# Revit family: Gira_5333100
name_source: partatom
category: Elektroinstallationen
revit_build: Autodesk Revit 2017 (Build: 20160225_1515(x64)
units: mm (PartAtom-declared; Revit-internal decimal feet)

## family parameters
Basisbauteil = Fläche
Beim Laden mit Abzugskörper schneiden = Nein
Bemaßung runder Anschluss = Durchmesser verwenden
Beschriftungsausrichtung beibehalten = Nein
Gemeinsam genutzt = Nein
Raumberechnungspunkt = Nein
Teiletyp = Normal

## types (1)
- Gira_5333100
    Andere Bussysteme = ohne
    Anzahl der Kanäle = 3
    Ausführung = Wandsender komplett
    Ausführung der Oberfläche = glänzend
    BIM = https://media.stage.bim.site und Tasten.rfa
    Bauelement = Sys55_Abdeckung_Schalten und Tasten
    Beschreibung = eNet Funk Wandsender 3fach System 55, Wippen mit Beschriftungsfeld Klar   Reinweiß glänzend Merkmale: - Die eNet Funksender übertragen Schalt-, Dimm-, und Jalousiefahrbefehle an entsprechende eNet Funkempfänger. - Problemlose Erweiterung vorhandener Schalterkombinationen. - Die Montage kann ohne Aufputz-Gehäuse oder Gerätedose erfolgen. - Auf Wänden kann der Funk Wandsender mittels Schrauben befestigt bzw. auf glatten oder transparenten Oberflächen mit einer Montageplatte aufgeklebt werden. - Übertragung von Schalt-, Dimm-, Jalousiefahr- und Szenenbefehlen. - Umschaltfunktion, optimiert für die Ansteuerung von Tastaktoren. - Wippe als Kanal- oder Szenenfunktion einstellbar. - 2-farbige LED rechts und links der Tasten zur Signalisierung. - Batteriebetriebenes Gerät. Mit eNet Server einstellbar:: - Vollverschlüsselte Funkübertragung (AES-CCM) ab eNet Server Software Version 2.0. - Signalisierung des Übertragungsstatus abschaltbar. - Bediensperren. - Szenen Alles-Ein bzw. Alles-Aus, Schwellwertszenen und individuelle Szenen konfigurierbar. - Konfiguration von Szenentaste über eNet SMART HOME app (Wenn-Dann-Regeln) zum Auslösen von Aktionen, Szenen, Zeitschaltuhren. - Update der Gerätesoftware. - Lokalisierung des Geräts.  Hinweise : - Batterien sind Verbrauchsgüter und müssen regelmäßig ersetzt werden. Bitte beachten Sie die Vorschriften zur Entsorgung von gebrauchten Batterien. - Der Funk Wandsender wird mit einer programmneutralen Inbetriebnahme-Wippe geliefert. Das passende Wippenset zum Schalterprogramm ist separat zu bestellen. - Bei Verwendung von Wippensets aus Metall und oder Abdeckrahmen aus Metall kann es zu Reichweiteneinbußen kommen.
    Bussystem Funkbus = Ja
    Bussystem KNX = Nein
    Bussystem KNX-Funk = Nein
    Bussystem LON = Nein
    Datenblatt = https://katalog.gira.de
    Farbe = weiß
    GTIN = 4010337116547
    HAN = 5333100
    Hersteller = Gira
    Mit Busankopplung = Nein
    Montageart = Aufputz
    Oberfläche = sonstige
    Produktseite = http://katalog.gira.de
    RAL-Nummer (ähnlich) = 9010
    Transparent = Nein
    Typname = Funk Dimmaktor 1f Mini 20 - 250 VA Gira eNet
    URL = https://www.gira.de
    Vorgabe-Ansicht = 1219 mm
    Werkstoff = sonstige
    Werkstoffgüte = sonstige

## geometry (parser evidence)
native form markers: Sweep x8
no freeform markers — native parametric forms only
